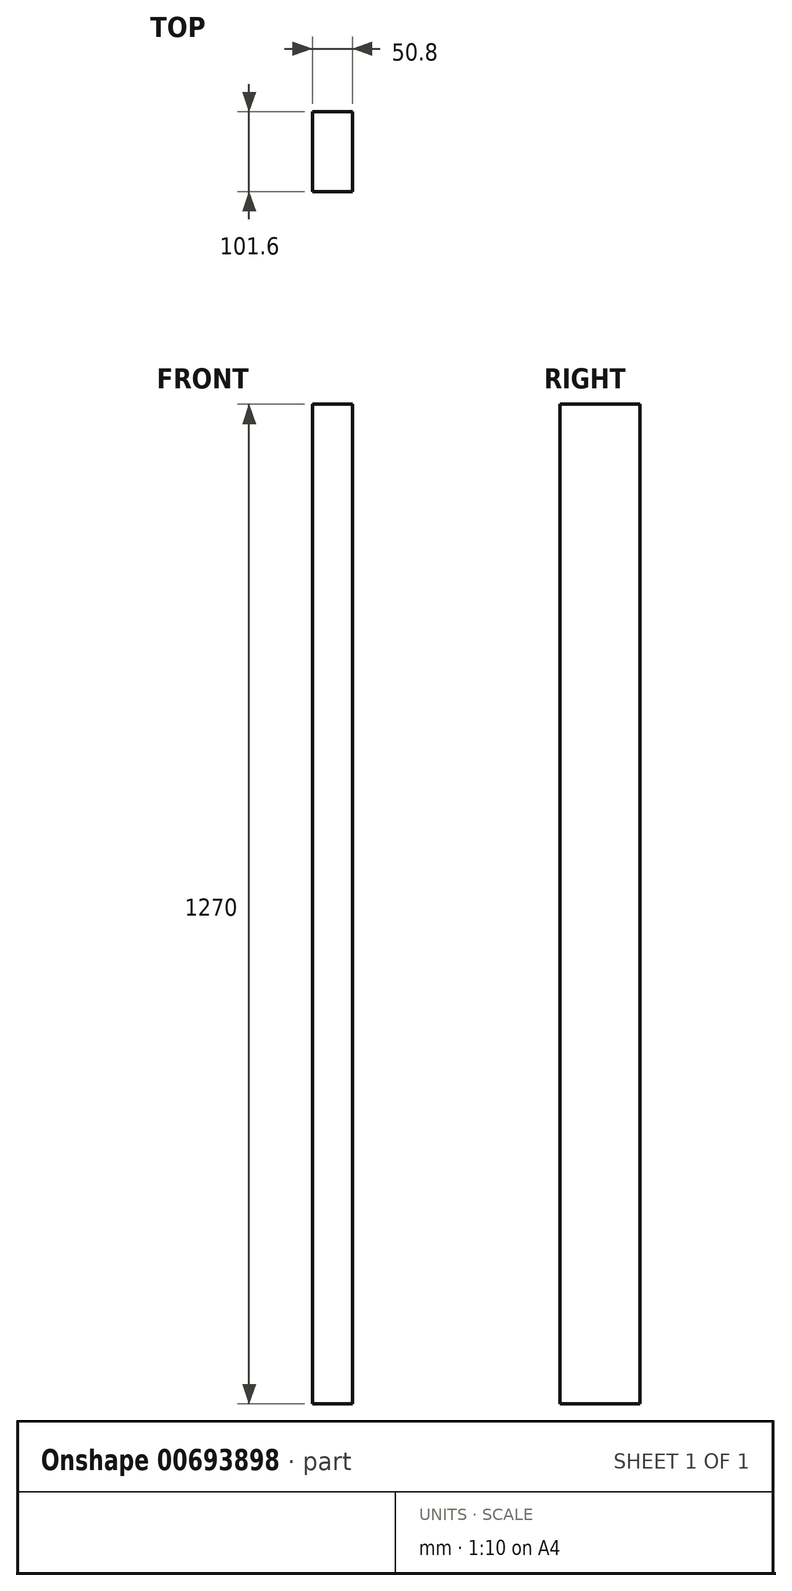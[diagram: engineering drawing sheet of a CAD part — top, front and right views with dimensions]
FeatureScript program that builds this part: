
annotation { "Feature Type Name" : "Feature", "Feature Type Description" : "" }
export const myFeature = defineFeature(function(context is Context, id is Id, definition is map)
    precondition{}
    {
        {
            var Q0;
            Q0=qCreatedBy(makeId("Top.planeOp"),FACE);
            var sketch = newSketch(context, id + "F0", { "sketchPlane" : qUnion([Q0])});
            skLineSegment(sketch, "E0.bottom", {"start": v(25.4, -50.8) * mm, "end": v(-25.4, -50.8) * mm});
            skLineSegment(sketch, "E0.top", {"start": v(25.4, 50.8) * mm, "end": v(-25.4, 50.8) * mm});
            skLineSegment(sketch, "E0.left", {"start": v(25.4, -50.8) * mm, "end": v(25.4, 50.8) * mm});
            skLineSegment(sketch, "E0.right", {"start": v(-25.4, -50.8) * mm, "end": v(-25.4, 50.8) * mm});
            skPoint(sketch, "E0.middle", {"position": v(0, 0) * mm});
            skSolve(sketch);
        }
        {
            var Q0;
            Q0=makeQuery(id+"F0.imprint","IMPRINT",FACE,{"disambiguationData":[TD([[makeQuery(id+"F0.imprint","IMPRINT",EDGE,{"derivedFrom":sQuery(id+"F0.wireOp",EDGE,"E0.bottom")}),-1.0]])]});
            extrude(context, id + "F1", {"entities" : qUnion([Q0]), "depth" : 1270 * mm, "offsetDistance" : 25.4 * mm});
        }
    });
